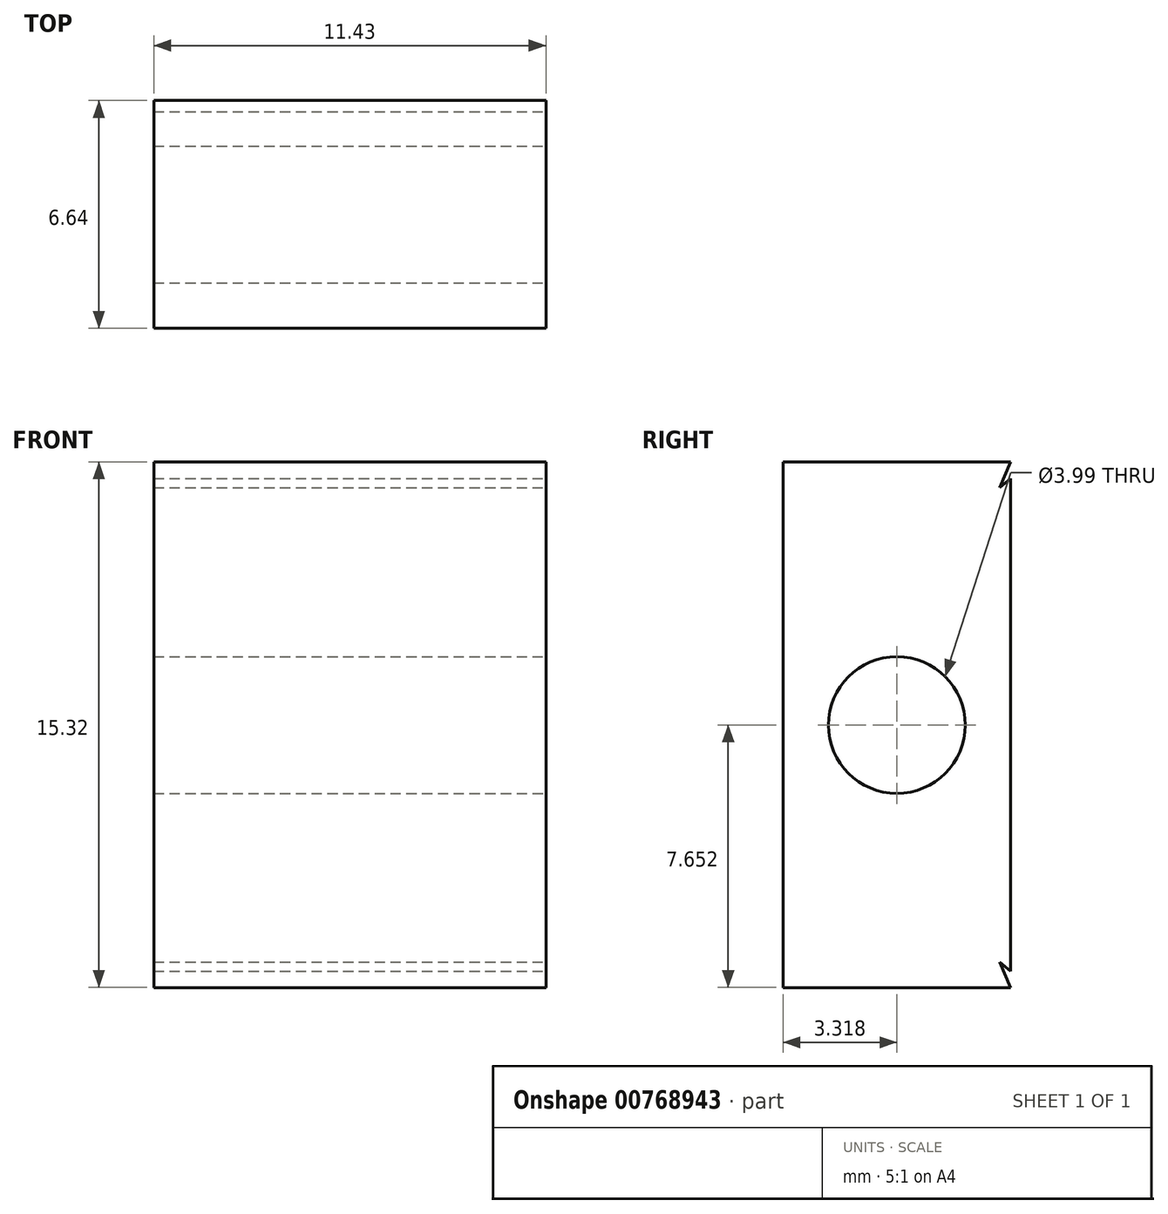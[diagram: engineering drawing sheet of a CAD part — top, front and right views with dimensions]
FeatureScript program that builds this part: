
annotation { "Feature Type Name" : "Feature", "Feature Type Description" : "" }
export const myFeature = defineFeature(function(context is Context, id is Id, definition is map)
    precondition{}
    {
        {
            var Q0;
            Q0=qCreatedBy(makeId("Right.planeOp"),FACE);
            var sketch = newSketch(context, id + "F0", { "sketchPlane" : qUnion([Q0])});
            skLineSegment(sketch, "E0.bottom", {"start": v(-16.3, 11.62) * mm, "end": v(14.88, 11.62) * mm});
            skLineSegment(sketch, "E0.top", {"start": v(-16.3, -17.59) * mm, "end": v(14.88, -17.59) * mm});
            skLineSegment(sketch, "E0.left", {"start": v(-16.3, 11.62) * mm, "end": v(-16.3, -17.59) * mm});
            skLineSegment(sketch, "E0.right", {"start": v(14.88, 11.62) * mm, "end": v(14.88, -17.59) * mm});
            skLineSegment(sketch, "E1", {"start": v(-16.3, -17.59) * mm, "end": v(-16.3, 7.81) * mm});
            skLineSegment(sketch, "E2", {"start": v(-16.3, 7.81) * mm, "end": v(14.88, 7.81) * mm});
            skLineSegment(sketch, "E3", {"start": v(14.88, 7.81) * mm, "end": v(14.88, -17.59) * mm});
            skLineSegment(sketch, "E4", {"start": v(-16.3, 7.81) * mm, "end": v(14.88, -17.59) * mm});
            skLineSegment(sketch, "E5", {"start": v(14.88, 7.81) * mm, "end": v(-16.3, -17.59) * mm});
            skLineSegment(sketch, "E6", {"start": v(-0.71, -4.89) * mm, "end": v(-0.71, -17.59) * mm});
            skLineSegment(sketch, "E7", {"start": v(-0.71, -4.89) * mm, "end": v(-0.71, 7.81) * mm});
            skLineSegment(sketch, "E8", {"start": v(-0.71, -17.59) * mm, "end": v(-11.7, -17.59) * mm});
            skLineSegment(sketch, "E9", {"start": v(-11.7, -17.59) * mm, "end": v(-11.7, 7.81) * mm});
            skLineSegment(sketch, "E10", {"start": v(-11.7, 7.81) * mm, "end": v(-0.71, 7.81) * mm});
            skLineSegment(sketch, "E11.MirrorCS", {"start": v(10.29, -17.59) * mm, "end": v(10.29, 7.81) * mm});
            skLineSegment(sketch, "E12.MirrorCS", {"start": v(-0.71, -17.59) * mm, "end": v(10.29, -17.59) * mm});
            skLineSegment(sketch, "E13", {"start": v(-0.71, 7.81) * mm, "end": v(10.29, -17.59) * mm});
            skLineSegment(sketch, "E14", {"start": v(10.29, 7.81) * mm, "end": v(-0.71, -17.59) * mm});
            skLineSegment(sketch, "E15", {"start": v(-0.71, -17.59) * mm, "end": v(-11.7, 7.81) * mm});
            skLineSegment(sketch, "E16", {"start": v(-0.71, 7.81) * mm, "end": v(-11.7, -17.59) * mm});
            skCircle(sketch, "E17", {"center": v(-6.21, -4.89) * mm, "radius": 2 * mm});
            skCircle(sketch, "E18", {"center": v(4.79, -4.89) * mm, "radius": 2 * mm});
            skLineSegment(sketch, "E19.bottom", {"start": v(-9.53, 2.78) * mm, "end": v(-2.9, 2.78) * mm});
            skLineSegment(sketch, "E19.top", {"start": v(-9.53, -12.54) * mm, "end": v(-2.9, -12.54) * mm});
            skLineSegment(sketch, "E19.left", {"start": v(-9.53, 2.78) * mm, "end": v(-9.53, -12.54) * mm});
            skLineSegment(sketch, "E19.right", {"start": v(-2.9, 2.78) * mm, "end": v(-2.9, -12.54) * mm});
            skLineSegment(sketch, "E20.MirrorCS", {"start": v(8.1, 2.78) * mm, "end": v(1.47, 2.78) * mm});
            skLineSegment(sketch, "E21.MirrorCS", {"start": v(1.47, 2.78) * mm, "end": v(1.47, -12.54) * mm});
            skLineSegment(sketch, "E22.MirrorCS", {"start": v(8.1, -12.54) * mm, "end": v(1.47, -12.54) * mm});
            skLineSegment(sketch, "E23.MirrorCS", {"start": v(8.1, 2.78) * mm, "end": v(8.1, -12.54) * mm});
            skLineSegment(sketch, "E24", {"start": v(-9.53, -12.54) * mm, "end": v(-2.9, -43.52) * mm});
            skLineSegment(sketch, "E25", {"start": v(-2.9, -43.52) * mm, "end": v(-2.9, -12.54) * mm});
            skLineSegment(sketch, "E26.MirrorCS", {"start": v(8.1, -12.54) * mm, "end": v(1.47, -43.52) * mm});
            skLineSegment(sketch, "E27.MirrorCS", {"start": v(1.47, -43.52) * mm, "end": v(1.47, -12.54) * mm});
            skSolve(sketch);
        }
        {
            var Q0;
            {var subQ0=sQuery(id+"F0.wireOp",EDGE,"E13");var subQ1=sQuery(id+"F0.wireOp",EDGE,"E5");var subQ2=makeQuery(id+"F0.imprint","INTERSECT",VERTEX,{"derivedFrom":[subQ1,subQ0]});Q0=makeQuery(id+"F0.imprint","IMPRINT",FACE,{"disambiguationData":[TD([[makeQuery(id+"F0.imprint","IMPRINT",EDGE,{"disambiguationData":[TD([[subQ2,-1.0]])],"derivedFrom":subQ1}),-1.0]])]});}
            var Q1;
            {var subQ0=sQuery(id+"F0.wireOp",EDGE,"E20.MirrorCS");Q1=makeQuery(id+"F0.imprint","IMPRINT",FACE,{"disambiguationData":[TD([[makeQuery(id+"F0.imprint","IMPRINT",EDGE,{"derivedFrom":subQ0}),1.0]])]});}
            var Q2;
            {var subQ5=sQuery(id+"F0.wireOp",EDGE,"E13");var subQ6=sQuery(id+"F0.wireOp",EDGE,"E4");var subQ7=makeQuery(id+"F0.imprint","INTERSECT",VERTEX,{"derivedFrom":[subQ6,subQ5]});Q2=makeQuery(id+"F0.imprint","IMPRINT",FACE,{"disambiguationData":[TD([[makeQuery(id+"F0.imprint","IMPRINT",EDGE,{"disambiguationData":[TD([[subQ7,-1.0]])],"derivedFrom":subQ6}),1.0]])]});}
            var Q3;
            {var subQ0=sQuery(id+"F0.wireOp",EDGE,"E14");var subQ1=sQuery(id+"F0.wireOp",EDGE,"E4");var subQ2=makeQuery(id+"F0.imprint","INTERSECT",VERTEX,{"derivedFrom":[subQ1,subQ0]});Q3=makeQuery(id+"F0.imprint","IMPRINT",FACE,{"disambiguationData":[TD([[makeQuery(id+"F0.imprint","IMPRINT",EDGE,{"disambiguationData":[TD([[subQ2,-1.0]])],"derivedFrom":subQ1}),-1.0]])]});}
            var Q4;
            {var subQ0=sQuery(id+"F0.wireOp",EDGE,"E21.MirrorCS");var subQ1=sQuery(id+"F0.wireOp",EDGE,"E4");var subQ2=makeQuery(id+"F0.imprint","INTERSECT",VERTEX,{"derivedFrom":[subQ1,subQ0]});Q4=makeQuery(id+"F0.imprint","IMPRINT",FACE,{"disambiguationData":[TD([[makeQuery(id+"F0.imprint","IMPRINT",EDGE,{"disambiguationData":[TD([[subQ2,-1.0]])],"derivedFrom":subQ1}),-1.0]])]});}
            var Q5;
            {var subQ0=sQuery(id+"F0.wireOp",EDGE,"E14");var subQ1=sQuery(id+"F0.wireOp",EDGE,"E4");var subQ2=makeQuery(id+"F0.imprint","INTERSECT",VERTEX,{"derivedFrom":[subQ1,subQ0]});Q5=makeQuery(id+"F0.imprint","IMPRINT",FACE,{"disambiguationData":[TD([[makeQuery(id+"F0.imprint","IMPRINT",EDGE,{"disambiguationData":[TD([[subQ2,-1.0]])],"derivedFrom":subQ1}),1.0]])]});}
            var Q6;
            {var subQ1=sQuery(id+"F0.wireOp",EDGE,"E4");var subQ9=sQuery(id+"F0.wireOp",EDGE,"E21.MirrorCS");var subQ11=makeQuery(id+"F0.imprint","INTERSECT",VERTEX,{"derivedFrom":[subQ1,subQ9]});Q6=makeQuery(id+"F0.imprint","IMPRINT",FACE,{"disambiguationData":[TD([[makeQuery(id+"F0.imprint","IMPRINT",EDGE,{"disambiguationData":[TD([[subQ11,-1.0]])],"derivedFrom":subQ1}),1.0]])]});}
            var Q7;
            {var subQ0=sQuery(id+"F0.wireOp",EDGE,"E14");var subQ1=sQuery(id+"F0.wireOp",EDGE,"E5");var subQ2=makeQuery(id+"F0.imprint","INTERSECT",VERTEX,{"derivedFrom":[subQ1,subQ0]});Q7=makeQuery(id+"F0.imprint","IMPRINT",FACE,{"disambiguationData":[TD([[makeQuery(id+"F0.imprint","IMPRINT",EDGE,{"disambiguationData":[TD([[subQ2,-1.0]])],"derivedFrom":subQ1}),1.0]])]});}
            var Q8;
            {var subQ0=sQuery(id+"F0.wireOp",EDGE,"E27.MirrorCS");var subQ1=sQuery(id+"F0.wireOp",EDGE,"E12.MirrorCS");var subQ2=makeQuery(id+"F0.imprint","INTERSECT",VERTEX,{"derivedFrom":[subQ1,subQ0]});Q8=makeQuery(id+"F0.imprint","IMPRINT",FACE,{"disambiguationData":[TD([[makeQuery(id+"F0.imprint","IMPRINT",EDGE,{"disambiguationData":[TD([[subQ2,-1.0]])],"derivedFrom":subQ1}),-1.0]])]});}
            var Q9;
            {var subQ5=sQuery(id+"F0.wireOp",EDGE,"E12.MirrorCS");var subQ7=sQuery(id+"F0.wireOp",EDGE,"E27.MirrorCS");var subQ9=makeQuery(id+"F0.imprint","INTERSECT",VERTEX,{"derivedFrom":[subQ5,subQ7]});Q9=makeQuery(id+"F0.imprint","IMPRINT",FACE,{"disambiguationData":[TD([[makeQuery(id+"F0.imprint","IMPRINT",EDGE,{"disambiguationData":[TD([[subQ9,-1.0]])],"derivedFrom":subQ5}),1.0]])]});}
            extrude(context, id + "F1", {"entities" : qUnion([Q0, Q1, Q2, Q3, Q4, Q5, Q6, Q7, Q8, Q9]), "oppositeDirection" : true, "depth" : 11.43 * mm, "offsetDistance" : 25.4 * mm});
        }
    });
